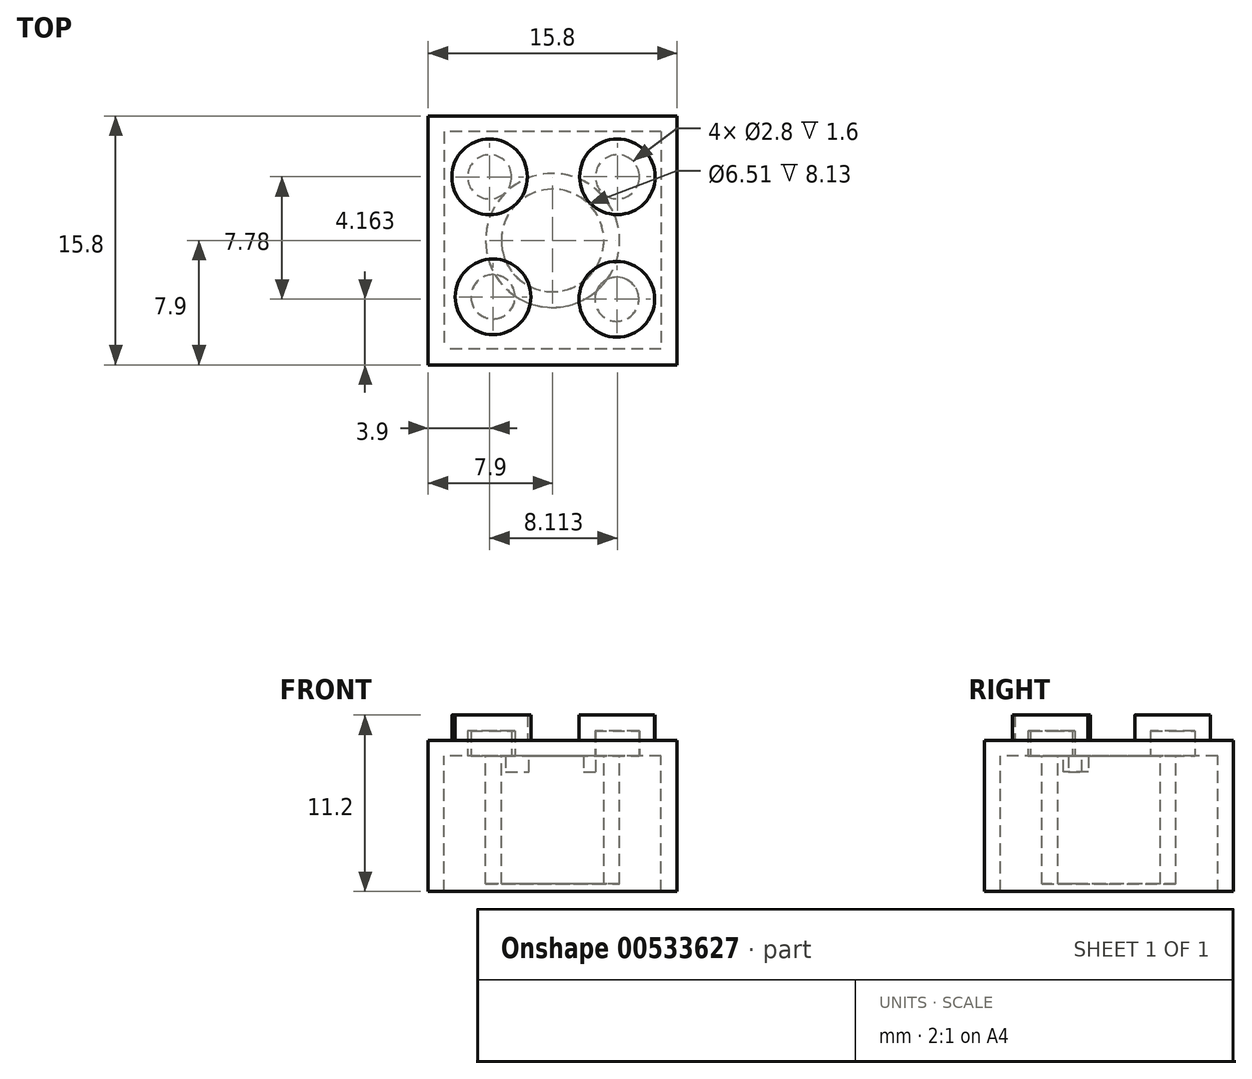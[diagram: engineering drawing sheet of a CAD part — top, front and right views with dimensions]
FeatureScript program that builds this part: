
annotation { "Feature Type Name" : "Feature", "Feature Type Description" : "" }
export const myFeature = defineFeature(function(context is Context, id is Id, definition is map)
    precondition{}
    {
        {
            var Q0;
            Q0=qCreatedBy(makeId("Top.planeOp"),FACE);
            var sketch = newSketch(context, id + "F0", { "sketchPlane" : qUnion([Q0])});
            skLineSegment(sketch, "E0.rect.bottom", {"start": v(7.9, 7.9) * mm, "end": v(-7.9, 7.9) * mm});
            skLineSegment(sketch, "E0.rect.top", {"start": v(7.9, -7.9) * mm, "end": v(-7.9, -7.9) * mm});
            skLineSegment(sketch, "E0.rect.left", {"start": v(7.9, 7.9) * mm, "end": v(7.9, -7.9) * mm});
            skLineSegment(sketch, "E0.rect.right", {"start": v(-7.9, 7.9) * mm, "end": v(-7.9, -7.9) * mm});
            skPoint(sketch, "E0.rect.middle", {"position": v(0, 0) * mm});
            skSolve(sketch);
        }
        {
            var Q0;
            Q0=makeQuery(id+"F0.imprint","IMPRINT",FACE,{"disambiguationData":[TD([[makeQuery(id+"F0.imprint","IMPRINT",EDGE,{"derivedFrom":sQuery(id+"F0.wireOp",EDGE,"E0.rect.bottom")}),1.0]])]});
            extrude(context, id + "F1", {"entities" : qUnion([Q0]), "oppositeDirection" : true, "depth" : 9.6 * mm, "offsetDistance" : 25 * mm});
        }
        {
            var Q0;
            Q0=makeQuery(id+"F0.imprint","IMPRINT",FACE,{"disambiguationData":[TD([[makeQuery(id+"F0.imprint","IMPRINT",EDGE,{"derivedFrom":sQuery(id+"F0.wireOp",EDGE,"E0.rect.bottom")}),1.0]])]});
            var sketch = newSketch(context, id + "F2", { "sketchPlane" : qUnion([Q0])});
            skCircle(sketch, "E1", {"center": v(-4, 4.04) * mm, "radius": 2.4 * mm});
            skSolve(sketch);
        }
        {
            var Q0;
            Q0=makeQuery(id+"F2.imprint","IMPRINT",FACE,{"disambiguationData":[TD([[makeQuery(id+"F2.imprint","IMPRINT",EDGE,{"derivedFrom":sQuery(id+"F2.wireOp",EDGE,"E1")}),-1.0]])]});
            var sketch = newSketch(context, id + "F3", { "sketchPlane" : qUnion([Q0])});
            skCircle(sketch, "E2", {"center": v(4.11, 4.04) * mm, "radius": 2.4 * mm});
            skSolve(sketch);
        }
        {
            var Q0;
            Q0=makeQuery(id+"F2.imprint","IMPRINT",FACE,{"disambiguationData":[TD([[makeQuery(id+"F2.imprint","IMPRINT",EDGE,{"derivedFrom":sQuery(id+"F2.wireOp",EDGE,"E1")}),-1.0]])]});
            var sketch = newSketch(context, id + "F4", { "sketchPlane" : qUnion([Q0])});
            skCircle(sketch, "E3", {"center": v(-3.78, -3.58) * mm, "radius": 2.4 * mm});
            skSolve(sketch);
        }
        {
            var Q0;
            Q0=makeQuery(id+"F0.imprint","IMPRINT",FACE,{"disambiguationData":[TD([[makeQuery(id+"F0.imprint","IMPRINT",EDGE,{"derivedFrom":sQuery(id+"F0.wireOp",EDGE,"E0.rect.bottom")}),1.0]])]});
            var sketch = newSketch(context, id + "F5", { "sketchPlane" : qUnion([Q0])});
            skCircle(sketch, "E4", {"center": v(4.08, -3.74) * mm, "radius": 2.4 * mm});
            skSolve(sketch);
        }
        {
            var Q0;
            Q0=makeQuery(id+"F4.imprint","IMPRINT",FACE,{"disambiguationData":[TD([[makeQuery(id+"F4.imprint","IMPRINT",EDGE,{"derivedFrom":sQuery(id+"F4.wireOp",EDGE,"E3")}),1.0]])]});
            extrude(context, id + "F6", {"entities" : qUnion([Q0]), "operationType" : NewBodyOperationType.ADD, "depth" : 1.6 * mm, "offsetDistance" : 25 * mm});
        }
        {
            var Q0;
            Q0=makeQuery(id+"F5.imprint","IMPRINT",FACE,{"disambiguationData":[TD([[makeQuery(id+"F5.imprint","IMPRINT",EDGE,{"derivedFrom":sQuery(id+"F5.wireOp",EDGE,"E4")}),1.0]])]});
            extrude(context, id + "F7", {"entities" : qUnion([Q0]), "operationType" : NewBodyOperationType.ADD, "depth" : 1.6 * mm, "offsetDistance" : 25 * mm});
        }
        {
            var Q0;
            Q0=makeQuery(id+"F3.imprint","IMPRINT",FACE,{"disambiguationData":[TD([[makeQuery(id+"F3.imprint","IMPRINT",EDGE,{"derivedFrom":sQuery(id+"F3.wireOp",EDGE,"E2")}),1.0]])]});
            extrude(context, id + "F8", {"entities" : qUnion([Q0]), "operationType" : NewBodyOperationType.ADD, "depth" : 1.6 * mm, "offsetDistance" : 25 * mm});
        }
        {
            var Q0;
            Q0=makeQuery(id+"F2.imprint","IMPRINT",FACE,{"disambiguationData":[TD([[makeQuery(id+"F2.imprint","IMPRINT",EDGE,{"derivedFrom":sQuery(id+"F2.wireOp",EDGE,"E1")}),1.0]])]});
            var Q1;
            Q1 = qSketchRegion(id + "F3", true);
            extrude(context, id + "F9", {"entities" : qUnion([Q0, Q1]), "operationType" : NewBodyOperationType.ADD, "depth" : 1.6 * mm, "offsetDistance" : 25 * mm});
        }
        {
            var Q0;
            Q0=makeQuery(id+"F1.opExtrude","CAP_FACE",FACE,{"disambiguationData":[OSD([sQuery(id+"F0.wireOp",EDGE,"E0.rect.bottom"),sQuery(id+"F0.wireOp",EDGE,"E0.rect.top"),sQuery(id+"F0.wireOp",EDGE,"E0.rect.left"),sQuery(id+"F0.wireOp",EDGE,"E0.rect.right")])],"isStart":false});
            shell(context, id + "F10", {"entities" : qUnion([Q0]), "thickness" : 1 * mm});
        }
        {
            var Q0;
            Q0=makeQuery(id+"F10.opShell","OFFSET_FACE",FACE,{"disambiguationData":[OSD([sQuery(id+"F0.wireOp",EDGE,"E0.rect.bottom"),sQuery(id+"F0.wireOp",EDGE,"E0.rect.top"),sQuery(id+"F0.wireOp",EDGE,"E0.rect.left"),sQuery(id+"F0.wireOp",EDGE,"E0.rect.right")])]});
            var sketch = newSketch(context, id + "F11", { "sketchPlane" : qUnion([Q0])});
            skCircle(sketch, "E5", {"center": v(0, 0) * mm, "radius": 4.25 * mm});
            skSolve(sketch);
        }
        {
            var Q0;
            Q0 = qSketchRegion(id + "F11", true);
            extrude(context, id + "F12", {"entities" : qUnion([Q0]), "operationType" : NewBodyOperationType.ADD, "depth" : 8.13 * mm, "offsetDistance" : 25 * mm});
        }
        {
            var Q0;
            Q0=makeQuery(id+"F12.opExtrude","CAP_FACE",FACE,{"disambiguationData":[OSD([sQuery(id+"F11.wireOp",EDGE,"E5")])],"isStart":false});
            shell(context, id + "F13", {"entities" : qUnion([Q0]), "thickness" : 1 * mm});
        }
    });
